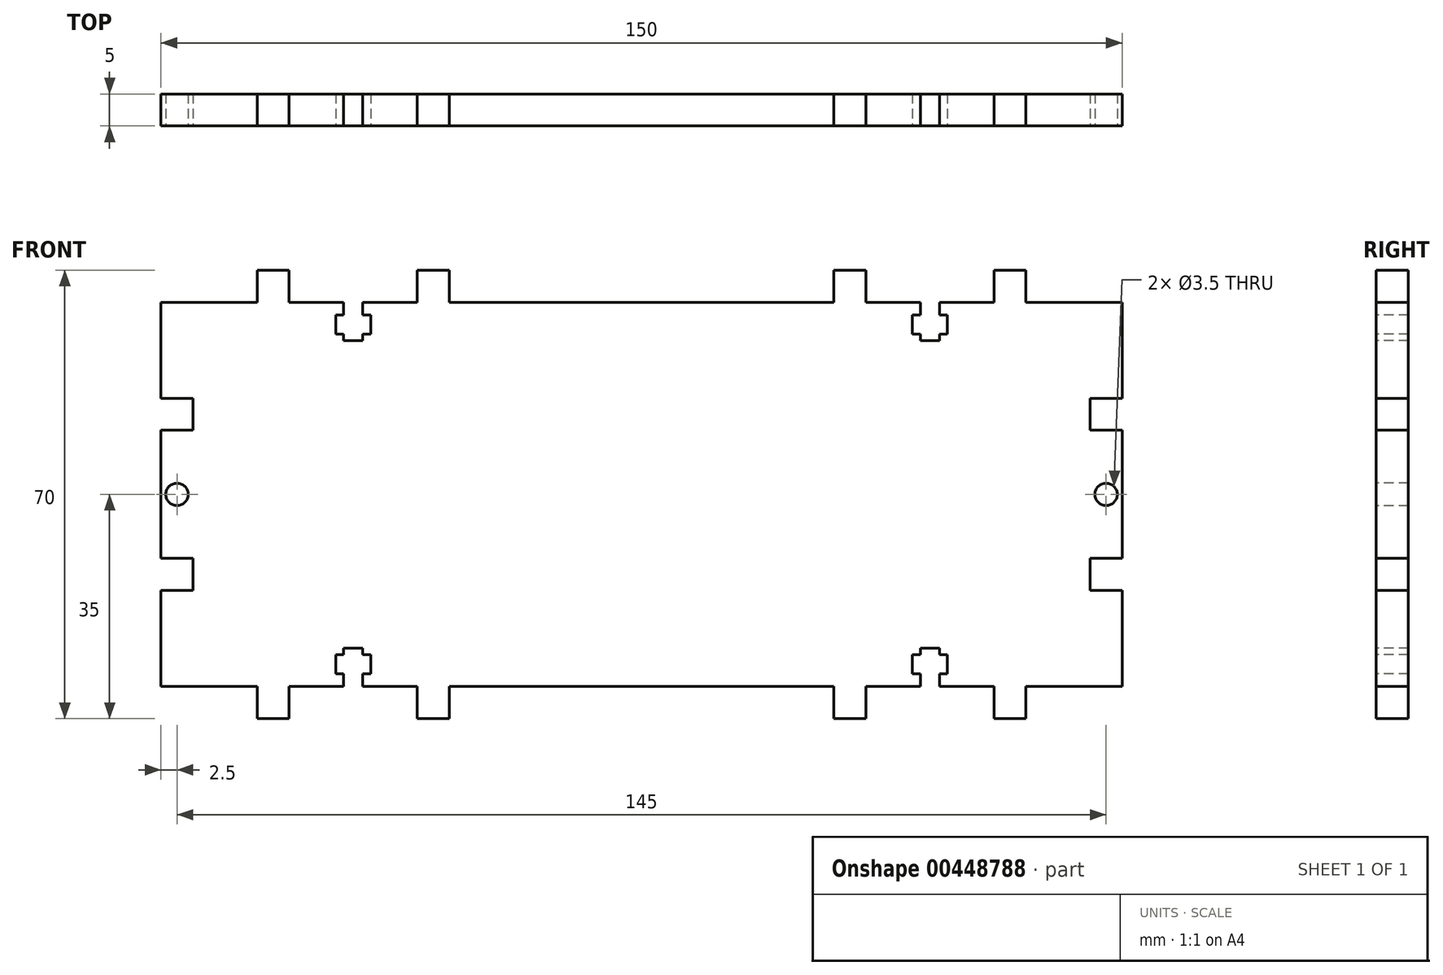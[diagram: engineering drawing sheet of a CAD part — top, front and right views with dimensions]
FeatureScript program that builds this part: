
annotation { "Feature Type Name" : "Feature", "Feature Type Description" : "" }
export const myFeature = defineFeature(function(context is Context, id is Id, definition is map)
    precondition{}
    {
        {
            var Q0;
            Q0=qCreatedBy(makeId("Top.planeOp"),FACE);
            var sketch = newSketch(context, id + "F0", { "sketchPlane" : qUnion([Q0])});
            skLineSegment(sketch, "E0.bottom", {"start": v(0, 0) * mm, "end": v(150, 0) * mm});
            skLineSegment(sketch, "E0.top", {"start": v(0, 5) * mm, "end": v(150, 5) * mm});
            skLineSegment(sketch, "E0.left", {"start": v(0, 0) * mm, "end": v(0, 5) * mm});
            skLineSegment(sketch, "E0.right", {"start": v(150, 0) * mm, "end": v(150, 5) * mm});
            skSolve(sketch);
        }
        {
            var Q0;
            Q0=makeQuery(id+"F0.imprint","IMPRINT",FACE,{"disambiguationData":[TD([[makeQuery(id+"F0.imprint","IMPRINT",EDGE,{"derivedFrom":sQuery(id+"F0.wireOp",EDGE,"E0.bottom")}),1.0]])]});
            extrude(context, id + "F1", {"entities" : qUnion([Q0]), "depth" : 60 * mm});
        }
        {
            var Q0;
            Q0=makeQuery(id+"F1.opExtrude","SWEPT_FACE",FACE,{"disambiguationData":[OSD([sQuery(id+"F0.wireOp",EDGE,"E0.bottom")])]});
            var sketch = newSketch(context, id + "F2", { "sketchPlane" : qUnion([Q0])});
            skLineSegment(sketch, "E1.bottom", {"start": v(15, 0) * mm, "end": v(20, 0) * mm});
            skLineSegment(sketch, "E1.top", {"start": v(15, -5) * mm, "end": v(20, -5) * mm});
            skLineSegment(sketch, "E1.left", {"start": v(15, 0) * mm, "end": v(15, -5) * mm});
            skLineSegment(sketch, "E1.right", {"start": v(20, 0) * mm, "end": v(20, -5) * mm});
            skLineSegment(sketch, "E2.bottom", {"start": v(40, 0) * mm, "end": v(45, 0) * mm});
            skLineSegment(sketch, "E2.top", {"start": v(40, -5) * mm, "end": v(45, -5) * mm});
            skLineSegment(sketch, "E2.left", {"start": v(40, 0) * mm, "end": v(40, -5) * mm});
            skLineSegment(sketch, "E2.right", {"start": v(45, 0) * mm, "end": v(45, -5) * mm});
            skLineSegment(sketch, "E3", {"start": v(75, 0) * mm, "end": v(75, 60) * mm, "construction": true});
            skLineSegment(sketch, "E4", {"start": v(0, 30) * mm, "end": v(150, 30) * mm, "construction": true});
            skLineSegment(sketch, "E5.MirrorCS", {"start": v(110, 0) * mm, "end": v(110, -5) * mm});
            skLineSegment(sketch, "E6.MirrorCS", {"start": v(105, 0) * mm, "end": v(105, -5) * mm});
            skLineSegment(sketch, "E7.MirrorCS", {"start": v(110, -5) * mm, "end": v(105, -5) * mm});
            skLineSegment(sketch, "E8.MirrorCS", {"start": v(110, 0) * mm, "end": v(105, 0) * mm});
            skLineSegment(sketch, "E9.MirrorCS", {"start": v(130, 0) * mm, "end": v(130, -5) * mm});
            skLineSegment(sketch, "E10.MirrorCS", {"start": v(135, 0) * mm, "end": v(135, -5) * mm});
            skLineSegment(sketch, "E11.MirrorCS", {"start": v(135, -5) * mm, "end": v(130, -5) * mm});
            skLineSegment(sketch, "E12.MirrorCS", {"start": v(135, 0) * mm, "end": v(130, 0) * mm});
            skLineSegment(sketch, "E13.MirrorCS", {"start": v(40, 60) * mm, "end": v(40, 65) * mm});
            skLineSegment(sketch, "E14.MirrorCS", {"start": v(40, 65) * mm, "end": v(45, 65) * mm});
            skLineSegment(sketch, "E15.MirrorCS", {"start": v(40, 60) * mm, "end": v(45, 60) * mm});
            skLineSegment(sketch, "E16.MirrorCS", {"start": v(20, 60) * mm, "end": v(20, 65) * mm});
            skLineSegment(sketch, "E17.MirrorCS", {"start": v(15, 60) * mm, "end": v(15, 65) * mm});
            skLineSegment(sketch, "E18.MirrorCS", {"start": v(15, 65) * mm, "end": v(20, 65) * mm});
            skLineSegment(sketch, "E19.MirrorCS", {"start": v(15, 60) * mm, "end": v(20, 60) * mm});
            skLineSegment(sketch, "E20.MirrorCS", {"start": v(135, 60) * mm, "end": v(135, 65) * mm});
            skLineSegment(sketch, "E21.MirrorCS", {"start": v(130, 60) * mm, "end": v(130, 65) * mm});
            skLineSegment(sketch, "E22.MirrorCS", {"start": v(110, 60) * mm, "end": v(105, 60) * mm});
            skLineSegment(sketch, "E23.MirrorCS", {"start": v(45, 60) * mm, "end": v(45, 65) * mm});
            skLineSegment(sketch, "E24.MirrorCS", {"start": v(135, 60) * mm, "end": v(130, 60) * mm});
            skLineSegment(sketch, "E25.MirrorCS", {"start": v(135, 65) * mm, "end": v(130, 65) * mm});
            skLineSegment(sketch, "E26.MirrorCS", {"start": v(110, 65) * mm, "end": v(105, 65) * mm});
            skLineSegment(sketch, "E27.MirrorCS", {"start": v(110, 60) * mm, "end": v(110, 65) * mm});
            skLineSegment(sketch, "E28.MirrorCS", {"start": v(105, 60) * mm, "end": v(105, 65) * mm});
            skSolve(sketch);
        }
        {
            var Q0;
            Q0=qSketchRegion(id+"F2",true);
            var Q1;
            Q1=makeQuery(id+"F1.opExtrude","SWEPT_FACE",FACE,{"disambiguationData":[OSD([sQuery(id+"F0.wireOp",EDGE,"E0.top")])]});
            extrude(context, id + "F3", {"entities" : qUnion([Q0]), "operationType" : NewBodyOperationType.ADD, "endBound" : BoundingType.UP_TO_SURFACE, "oppositeDirection" : true, "endBoundEntityFace" : qUnion([Q1]), "depth" : 25 * mm});
        }
        {
            var Q0;
            Q0=makeQuery(id+"F3.boolean.opBoolean","MERGE",FACE,{"derivedFrom":[makeQuery(id+"F1.opExtrude","SWEPT_FACE",FACE,{"disambiguationData":[OSD([sQuery(id+"F0.wireOp",EDGE,"E0.bottom")])]}),makeQuery(id+"F3.opExtrude","CAP_FACE",FACE,{"disambiguationData":[OSD([sQuery(id+"F2.wireOp",EDGE,"E1.bottom"),sQuery(id+"F2.wireOp",EDGE,"E1.top"),sQuery(id+"F2.wireOp",EDGE,"E1.left"),sQuery(id+"F2.wireOp",EDGE,"E1.right")])],"isStart":true}),makeQuery(id+"F3.opExtrude","CAP_FACE",FACE,{"disambiguationData":[OSD([sQuery(id+"F2.wireOp",EDGE,"E2.bottom"),sQuery(id+"F2.wireOp",EDGE,"E2.top"),sQuery(id+"F2.wireOp",EDGE,"E2.left"),sQuery(id+"F2.wireOp",EDGE,"E2.right")])],"isStart":true}),makeQuery(id+"F3.opExtrude","CAP_FACE",FACE,{"disambiguationData":[OSD([sQuery(id+"F2.wireOp",EDGE,"E5.MirrorCS"),sQuery(id+"F2.wireOp",EDGE,"E6.MirrorCS"),sQuery(id+"F2.wireOp",EDGE,"E7.MirrorCS"),sQuery(id+"F2.wireOp",EDGE,"E8.MirrorCS")])],"isStart":true}),makeQuery(id+"F3.opExtrude","CAP_FACE",FACE,{"disambiguationData":[OSD([sQuery(id+"F2.wireOp",EDGE,"E9.MirrorCS"),sQuery(id+"F2.wireOp",EDGE,"E10.MirrorCS"),sQuery(id+"F2.wireOp",EDGE,"E11.MirrorCS"),sQuery(id+"F2.wireOp",EDGE,"E12.MirrorCS")])],"isStart":true}),makeQuery(id+"F3.opExtrude","CAP_FACE",FACE,{"disambiguationData":[OSD([sQuery(id+"F2.wireOp",EDGE,"E13.MirrorCS"),sQuery(id+"F2.wireOp",EDGE,"E14.MirrorCS"),sQuery(id+"F2.wireOp",EDGE,"E15.MirrorCS"),sQuery(id+"F2.wireOp",EDGE,"E23.MirrorCS")])],"isStart":true}),makeQuery(id+"F3.opExtrude","CAP_FACE",FACE,{"disambiguationData":[OSD([sQuery(id+"F2.wireOp",EDGE,"E16.MirrorCS"),sQuery(id+"F2.wireOp",EDGE,"E17.MirrorCS"),sQuery(id+"F2.wireOp",EDGE,"E18.MirrorCS"),sQuery(id+"F2.wireOp",EDGE,"E19.MirrorCS")])],"isStart":true}),makeQuery(id+"F3.opExtrude","CAP_FACE",FACE,{"disambiguationData":[OSD([sQuery(id+"F2.wireOp",EDGE,"E20.MirrorCS"),sQuery(id+"F2.wireOp",EDGE,"E21.MirrorCS"),sQuery(id+"F2.wireOp",EDGE,"E24.MirrorCS"),sQuery(id+"F2.wireOp",EDGE,"E25.MirrorCS")])],"isStart":true}),makeQuery(id+"F3.opExtrude","CAP_FACE",FACE,{"disambiguationData":[OSD([sQuery(id+"F2.wireOp",EDGE,"E22.MirrorCS"),sQuery(id+"F2.wireOp",EDGE,"E26.MirrorCS"),sQuery(id+"F2.wireOp",EDGE,"E27.MirrorCS"),sQuery(id+"F2.wireOp",EDGE,"E28.MirrorCS")])],"isStart":true}),makeQuery(id+"F3.opExtrude","CAP_FACE",FACE,{"disambiguationData":[OSD([sQuery(id+"F2.wireOp",EDGE,"a409461e-9a6c-40b4-bf51-24f98c17385d.bottom"),sQuery(id+"F2.wireOp",EDGE,"a409461e-9a6c-40b4-bf51-24f98c17385d.top"),sQuery(id+"F2.wireOp",EDGE,"a409461e-9a6c-40b4-bf51-24f98c17385d.left"),sQuery(id+"F2.wireOp",EDGE,"a409461e-9a6c-40b4-bf51-24f98c17385d.right")])],"isStart":true}),makeQuery(id+"F3.opExtrude","CAP_FACE",FACE,{"disambiguationData":[OSD([sQuery(id+"F2.wireOp",EDGE,"da60d496-b721-4d9c-8835-50d6b0d56d3c.bottom"),sQuery(id+"F2.wireOp",EDGE,"da60d496-b721-4d9c-8835-50d6b0d56d3c.top"),sQuery(id+"F2.wireOp",EDGE,"da60d496-b721-4d9c-8835-50d6b0d56d3c.left"),sQuery(id+"F2.wireOp",EDGE,"da60d496-b721-4d9c-8835-50d6b0d56d3c.right")])],"isStart":true}),makeQuery(id+"F3.opExtrude","CAP_FACE",FACE,{"disambiguationData":[OSD([sQuery(id+"F2.wireOp",EDGE,"2704353c-3130-41fa-bc24-460208ad23760.MirrorCS"),sQuery(id+"F2.wireOp",EDGE,"2704353c-3130-41fa-bc24-460208ad23764.MirrorCS"),sQuery(id+"F2.wireOp",EDGE,"2704353c-3130-41fa-bc24-460208ad23765.MirrorCS"),sQuery(id+"F2.wireOp",EDGE,"2704353c-3130-41fa-bc24-460208ad23766.MirrorCS")])],"isStart":true}),makeQuery(id+"F3.opExtrude","CAP_FACE",FACE,{"disambiguationData":[OSD([sQuery(id+"F2.wireOp",EDGE,"2704353c-3130-41fa-bc24-460208ad23761.MirrorCS"),sQuery(id+"F2.wireOp",EDGE,"2704353c-3130-41fa-bc24-460208ad23762.MirrorCS"),sQuery(id+"F2.wireOp",EDGE,"2704353c-3130-41fa-bc24-460208ad23763.MirrorCS"),sQuery(id+"F2.wireOp",EDGE,"2704353c-3130-41fa-bc24-460208ad23767.MirrorCS")])],"isStart":true})]});
            var sketch = newSketch(context, id + "F4", { "sketchPlane" : qUnion([Q0])});
            skLineSegment(sketch, "E29", {"start": v(75, 60) * mm, "end": v(75, 0) * mm, "construction": true});
            skLineSegment(sketch, "E30", {"start": v(0, 30) * mm, "end": v(150, 30) * mm, "construction": true});
            skLineSegment(sketch, "E31.bottom", {"start": v(28.5, 0) * mm, "end": v(31.5, 0) * mm});
            skLineSegment(sketch, "E31.top", {"start": v(28.5, 6) * mm, "end": v(31.5, 6) * mm});
            skLineSegment(sketch, "E31.left", {"start": v(28.5, 0) * mm, "end": v(28.5, 2) * mm});
            skLineSegment(sketch, "E31.right", {"start": v(31.5, 0) * mm, "end": v(31.5, 2) * mm});
            skPoint(sketch, "E32", {"position": v(30, 0) * mm});
            skLineSegment(sketch, "E33.bottom", {"start": v(27.25, 5) * mm, "end": v(28.5, 5) * mm});
            skLineSegment(sketch, "E33.top", {"start": v(27.25, 2) * mm, "end": v(28.5, 2) * mm});
            skLineSegment(sketch, "E33.left", {"start": v(27.25, 5) * mm, "end": v(27.25, 2) * mm});
            skLineSegment(sketch, "E33.right", {"start": v(32.75, 5) * mm, "end": v(32.75, 2) * mm});
            skLineSegment(sketch, "E34.trimOffspring", {"start": v(28.5, 5) * mm, "end": v(28.5, 6) * mm});
            skLineSegment(sketch, "E35.trimOffspring", {"start": v(31.5, 5) * mm, "end": v(31.5, 6) * mm});
            skLineSegment(sketch, "E36.trimOffspring", {"start": v(31.5, 5) * mm, "end": v(32.75, 5) * mm});
            skLineSegment(sketch, "E37.trimOffspring", {"start": v(31.5, 2) * mm, "end": v(32.75, 2) * mm});
            skPoint(sketch, "E38", {"position": v(30, 6) * mm});
            skLineSegment(sketch, "E39.MirrorCS", {"start": v(118.5, 5) * mm, "end": v(117.25, 5) * mm});
            skLineSegment(sketch, "E40.MirrorCS", {"start": v(121.5, 5) * mm, "end": v(121.5, 6) * mm});
            skLineSegment(sketch, "E41.MirrorCS", {"start": v(118.5, 5) * mm, "end": v(118.5, 6) * mm});
            skLineSegment(sketch, "E42.MirrorCS", {"start": v(122.75, 2) * mm, "end": v(121.5, 2) * mm});
            skLineSegment(sketch, "E43.MirrorCS", {"start": v(122.75, 5) * mm, "end": v(121.5, 5) * mm});
            skLineSegment(sketch, "E44.MirrorCS", {"start": v(118.5, 0) * mm, "end": v(118.5, 2) * mm});
            skLineSegment(sketch, "E45.MirrorCS", {"start": v(121.5, 0) * mm, "end": v(121.5, 2) * mm});
            skLineSegment(sketch, "E46.MirrorCS", {"start": v(118.5, 2) * mm, "end": v(117.25, 2) * mm});
            skLineSegment(sketch, "E47.MirrorCS", {"start": v(121.5, 6) * mm, "end": v(118.5, 6) * mm});
            skLineSegment(sketch, "E48.MirrorCS", {"start": v(121.5, 0) * mm, "end": v(118.5, 0) * mm});
            skPoint(sketch, "E49.MirrorP", {"position": v(120, 6) * mm});
            skLineSegment(sketch, "E50.MirrorCS", {"start": v(122.75, 5) * mm, "end": v(122.75, 2) * mm});
            skLineSegment(sketch, "E51.MirrorCS", {"start": v(117.25, 5) * mm, "end": v(117.25, 2) * mm});
            skPoint(sketch, "E52.MirrorP", {"position": v(120, 0) * mm});
            skLineSegment(sketch, "E53.MirrorCS", {"start": v(122.75, 55) * mm, "end": v(121.5, 55) * mm});
            skLineSegment(sketch, "E54.MirrorCS", {"start": v(31.5, 55) * mm, "end": v(32.75, 55) * mm});
            skLineSegment(sketch, "E55.MirrorCS", {"start": v(31.5, 55) * mm, "end": v(31.5, 54) * mm});
            skLineSegment(sketch, "E56.MirrorCS", {"start": v(28.5, 55) * mm, "end": v(28.5, 54) * mm});
            skLineSegment(sketch, "E57.MirrorCS", {"start": v(27.25, 58) * mm, "end": v(28.5, 58) * mm});
            skLineSegment(sketch, "E58.MirrorCS", {"start": v(27.25, 55) * mm, "end": v(28.5, 55) * mm});
            skLineSegment(sketch, "E59.MirrorCS", {"start": v(31.5, 60) * mm, "end": v(31.5, 58) * mm});
            skLineSegment(sketch, "E60.MirrorCS", {"start": v(28.5, 60) * mm, "end": v(28.5, 58) * mm});
            skLineSegment(sketch, "E61.MirrorCS", {"start": v(28.5, 54) * mm, "end": v(31.5, 54) * mm});
            skLineSegment(sketch, "E62.MirrorCS", {"start": v(28.5, 60) * mm, "end": v(31.5, 60) * mm});
            skLineSegment(sketch, "E63.MirrorCS", {"start": v(118.5, 60) * mm, "end": v(118.5, 58) * mm});
            skLineSegment(sketch, "E64.MirrorCS", {"start": v(118.5, 55) * mm, "end": v(118.5, 54) * mm});
            skLineSegment(sketch, "E65.MirrorCS", {"start": v(121.5, 60) * mm, "end": v(121.5, 58) * mm});
            skLineSegment(sketch, "E66.MirrorCS", {"start": v(31.5, 58) * mm, "end": v(32.75, 58) * mm});
            skLineSegment(sketch, "E67.MirrorCS", {"start": v(118.5, 58) * mm, "end": v(117.25, 58) * mm});
            skLineSegment(sketch, "E68.MirrorCS", {"start": v(122.75, 58) * mm, "end": v(121.5, 58) * mm});
            skLineSegment(sketch, "E69.MirrorCS", {"start": v(118.5, 55) * mm, "end": v(117.25, 55) * mm});
            skLineSegment(sketch, "E70.MirrorCS", {"start": v(121.5, 55) * mm, "end": v(121.5, 54) * mm});
            skLineSegment(sketch, "E71.MirrorCS", {"start": v(121.5, 54) * mm, "end": v(118.5, 54) * mm});
            skLineSegment(sketch, "E72.MirrorCS", {"start": v(121.5, 60) * mm, "end": v(118.5, 60) * mm});
            skLineSegment(sketch, "E73.MirrorCS", {"start": v(117.25, 55) * mm, "end": v(117.25, 58) * mm});
            skLineSegment(sketch, "E74.MirrorCS", {"start": v(32.75, 55) * mm, "end": v(32.75, 58) * mm});
            skLineSegment(sketch, "E75.MirrorCS", {"start": v(27.25, 55) * mm, "end": v(27.25, 58) * mm});
            skPoint(sketch, "E76.MirrorP", {"position": v(120, 54) * mm});
            skPoint(sketch, "E77.MirrorP", {"position": v(30, 60) * mm});
            skPoint(sketch, "E78.MirrorP", {"position": v(120, 60) * mm});
            skPoint(sketch, "E79.MirrorP", {"position": v(30, 54) * mm});
            skLineSegment(sketch, "E80.MirrorCS", {"start": v(122.75, 55) * mm, "end": v(122.75, 58) * mm});
            skPoint(sketch, "E81", {"position": v(0, 30) * mm});
            skPoint(sketch, "E82.MirrorP", {"position": v(150, 30) * mm});
            skCircle(sketch, "E83", {"center": v(2.5, 30) * mm, "radius": 1.75 * mm});
            skLineSegment(sketch, "E84.bottom", {"start": v(0, 45) * mm, "end": v(5, 45) * mm});
            skLineSegment(sketch, "E84.top", {"start": v(0, 40) * mm, "end": v(5, 40) * mm});
            skLineSegment(sketch, "E84.left", {"start": v(0, 45) * mm, "end": v(0, 40) * mm});
            skLineSegment(sketch, "E84.right", {"start": v(5, 45) * mm, "end": v(5, 40) * mm});
            skPoint(sketch, "E85", {"position": v(2.5, 40) * mm});
            skLineSegment(sketch, "E86.MirrorCS", {"start": v(0, 20) * mm, "end": v(5, 20) * mm});
            skLineSegment(sketch, "E87.MirrorCS", {"start": v(5, 15) * mm, "end": v(5, 20) * mm});
            skLineSegment(sketch, "E88.MirrorCS", {"start": v(0, 15) * mm, "end": v(5, 15) * mm});
            skLineSegment(sketch, "E89.MirrorCS", {"start": v(0, 15) * mm, "end": v(0, 20) * mm});
            skLineSegment(sketch, "E90.MirrorCS", {"start": v(145, 45) * mm, "end": v(145, 40) * mm});
            skLineSegment(sketch, "E91.MirrorCS", {"start": v(150, 45) * mm, "end": v(150, 40) * mm});
            skLineSegment(sketch, "E92.MirrorCS", {"start": v(150, 45) * mm, "end": v(145, 45) * mm});
            skLineSegment(sketch, "E93.MirrorCS", {"start": v(150, 40) * mm, "end": v(145, 40) * mm});
            skCircle(sketch, "E94.MirrorC", {"center": v(147.5, 30) * mm, "radius": 1.75 * mm});
            skLineSegment(sketch, "E95.MirrorCS", {"start": v(145, 15) * mm, "end": v(145, 20) * mm});
            skLineSegment(sketch, "E96.MirrorCS", {"start": v(150, 15) * mm, "end": v(145, 15) * mm});
            skLineSegment(sketch, "E97.MirrorCS", {"start": v(150, 20) * mm, "end": v(145, 20) * mm});
            skLineSegment(sketch, "E98.MirrorCS", {"start": v(150, 15) * mm, "end": v(150, 20) * mm});
            skSolve(sketch);
        }
        {
            var Q0;
            Q0=qSketchRegion(id+"F4",true);
            var Q1;
            {var subQ0=sQuery(id+"F0.wireOp",EDGE,"E0.top");Q1=makeQuery(id+"F3.boolean.opBoolean","MERGE",FACE,{"derivedFrom":[makeQuery(id+"F1.opExtrude","SWEPT_FACE",FACE,{"disambiguationData":[OSD([subQ0])]}),makeQuery(id+"F3.opExtrude","CAP_FACE",FACE,{"disambiguationData":[OSD([subQ0]),ownerDisambiguation([makeQuery(id+"F3.opExtrude","SWEPT_BODY",BODY,{"disambiguationData":[OSD([sQuery(id+"F2.wireOp",EDGE,"E1.bottom"),sQuery(id+"F2.wireOp",EDGE,"E1.top"),sQuery(id+"F2.wireOp",EDGE,"E1.left"),sQuery(id+"F2.wireOp",EDGE,"E1.right")])]})])],"isStart":false}),makeQuery(id+"F3.opExtrude","CAP_FACE",FACE,{"disambiguationData":[OSD([subQ0]),ownerDisambiguation([makeQuery(id+"F3.opExtrude","SWEPT_BODY",BODY,{"disambiguationData":[OSD([sQuery(id+"F2.wireOp",EDGE,"E2.bottom"),sQuery(id+"F2.wireOp",EDGE,"E2.top"),sQuery(id+"F2.wireOp",EDGE,"E2.left"),sQuery(id+"F2.wireOp",EDGE,"E2.right")])]})])],"isStart":false}),makeQuery(id+"F3.opExtrude","CAP_FACE",FACE,{"disambiguationData":[OSD([subQ0]),ownerDisambiguation([makeQuery(id+"F3.opExtrude","SWEPT_BODY",BODY,{"disambiguationData":[OSD([sQuery(id+"F2.wireOp",EDGE,"E5.MirrorCS"),sQuery(id+"F2.wireOp",EDGE,"E6.MirrorCS"),sQuery(id+"F2.wireOp",EDGE,"E7.MirrorCS"),sQuery(id+"F2.wireOp",EDGE,"E8.MirrorCS")])]})])],"isStart":false}),makeQuery(id+"F3.opExtrude","CAP_FACE",FACE,{"disambiguationData":[OSD([subQ0]),ownerDisambiguation([makeQuery(id+"F3.opExtrude","SWEPT_BODY",BODY,{"disambiguationData":[OSD([sQuery(id+"F2.wireOp",EDGE,"E9.MirrorCS"),sQuery(id+"F2.wireOp",EDGE,"E10.MirrorCS"),sQuery(id+"F2.wireOp",EDGE,"E11.MirrorCS"),sQuery(id+"F2.wireOp",EDGE,"E12.MirrorCS")])]})])],"isStart":false}),makeQuery(id+"F3.opExtrude","CAP_FACE",FACE,{"disambiguationData":[OSD([subQ0]),ownerDisambiguation([makeQuery(id+"F3.opExtrude","SWEPT_BODY",BODY,{"disambiguationData":[OSD([sQuery(id+"F2.wireOp",EDGE,"E13.MirrorCS"),sQuery(id+"F2.wireOp",EDGE,"E14.MirrorCS"),sQuery(id+"F2.wireOp",EDGE,"E15.MirrorCS"),sQuery(id+"F2.wireOp",EDGE,"E23.MirrorCS")])]})])],"isStart":false}),makeQuery(id+"F3.opExtrude","CAP_FACE",FACE,{"disambiguationData":[OSD([subQ0]),ownerDisambiguation([makeQuery(id+"F3.opExtrude","SWEPT_BODY",BODY,{"disambiguationData":[OSD([sQuery(id+"F2.wireOp",EDGE,"E16.MirrorCS"),sQuery(id+"F2.wireOp",EDGE,"E17.MirrorCS"),sQuery(id+"F2.wireOp",EDGE,"E18.MirrorCS"),sQuery(id+"F2.wireOp",EDGE,"E19.MirrorCS")])]})])],"isStart":false}),makeQuery(id+"F3.opExtrude","CAP_FACE",FACE,{"disambiguationData":[OSD([subQ0]),ownerDisambiguation([makeQuery(id+"F3.opExtrude","SWEPT_BODY",BODY,{"disambiguationData":[OSD([sQuery(id+"F2.wireOp",EDGE,"E20.MirrorCS"),sQuery(id+"F2.wireOp",EDGE,"E21.MirrorCS"),sQuery(id+"F2.wireOp",EDGE,"E24.MirrorCS"),sQuery(id+"F2.wireOp",EDGE,"E25.MirrorCS")])]})])],"isStart":false}),makeQuery(id+"F3.opExtrude","CAP_FACE",FACE,{"disambiguationData":[OSD([subQ0]),ownerDisambiguation([makeQuery(id+"F3.opExtrude","SWEPT_BODY",BODY,{"disambiguationData":[OSD([sQuery(id+"F2.wireOp",EDGE,"E22.MirrorCS"),sQuery(id+"F2.wireOp",EDGE,"E26.MirrorCS"),sQuery(id+"F2.wireOp",EDGE,"E27.MirrorCS"),sQuery(id+"F2.wireOp",EDGE,"E28.MirrorCS")])]})])],"isStart":false}),makeQuery(id+"F3.opExtrude","CAP_FACE",FACE,{"disambiguationData":[OSD([subQ0]),ownerDisambiguation([makeQuery(id+"F3.opExtrude","SWEPT_BODY",BODY,{"disambiguationData":[OSD([sQuery(id+"F2.wireOp",EDGE,"a409461e-9a6c-40b4-bf51-24f98c17385d.bottom"),sQuery(id+"F2.wireOp",EDGE,"a409461e-9a6c-40b4-bf51-24f98c17385d.top"),sQuery(id+"F2.wireOp",EDGE,"a409461e-9a6c-40b4-bf51-24f98c17385d.left"),sQuery(id+"F2.wireOp",EDGE,"a409461e-9a6c-40b4-bf51-24f98c17385d.right")])]})])],"isStart":false}),makeQuery(id+"F3.opExtrude","CAP_FACE",FACE,{"disambiguationData":[OSD([subQ0]),ownerDisambiguation([makeQuery(id+"F3.opExtrude","SWEPT_BODY",BODY,{"disambiguationData":[OSD([sQuery(id+"F2.wireOp",EDGE,"da60d496-b721-4d9c-8835-50d6b0d56d3c.bottom"),sQuery(id+"F2.wireOp",EDGE,"da60d496-b721-4d9c-8835-50d6b0d56d3c.top"),sQuery(id+"F2.wireOp",EDGE,"da60d496-b721-4d9c-8835-50d6b0d56d3c.left"),sQuery(id+"F2.wireOp",EDGE,"da60d496-b721-4d9c-8835-50d6b0d56d3c.right")])]})])],"isStart":false}),makeQuery(id+"F3.opExtrude","CAP_FACE",FACE,{"disambiguationData":[OSD([subQ0]),ownerDisambiguation([makeQuery(id+"F3.opExtrude","SWEPT_BODY",BODY,{"disambiguationData":[OSD([sQuery(id+"F2.wireOp",EDGE,"2704353c-3130-41fa-bc24-460208ad23760.MirrorCS"),sQuery(id+"F2.wireOp",EDGE,"2704353c-3130-41fa-bc24-460208ad23764.MirrorCS"),sQuery(id+"F2.wireOp",EDGE,"2704353c-3130-41fa-bc24-460208ad23765.MirrorCS"),sQuery(id+"F2.wireOp",EDGE,"2704353c-3130-41fa-bc24-460208ad23766.MirrorCS")])]})])],"isStart":false}),makeQuery(id+"F3.opExtrude","CAP_FACE",FACE,{"disambiguationData":[OSD([subQ0]),ownerDisambiguation([makeQuery(id+"F3.opExtrude","SWEPT_BODY",BODY,{"disambiguationData":[OSD([sQuery(id+"F2.wireOp",EDGE,"2704353c-3130-41fa-bc24-460208ad23761.MirrorCS"),sQuery(id+"F2.wireOp",EDGE,"2704353c-3130-41fa-bc24-460208ad23762.MirrorCS"),sQuery(id+"F2.wireOp",EDGE,"2704353c-3130-41fa-bc24-460208ad23763.MirrorCS"),sQuery(id+"F2.wireOp",EDGE,"2704353c-3130-41fa-bc24-460208ad23767.MirrorCS")])]})])],"isStart":false})]});}
            extrude(context, id + "F5", {"entities" : qUnion([Q0]), "operationType" : NewBodyOperationType.REMOVE, "endBound" : BoundingType.UP_TO_SURFACE, "oppositeDirection" : true, "endBoundEntityFace" : qUnion([Q1]), "depth" : 25 * mm});
        }
    });
